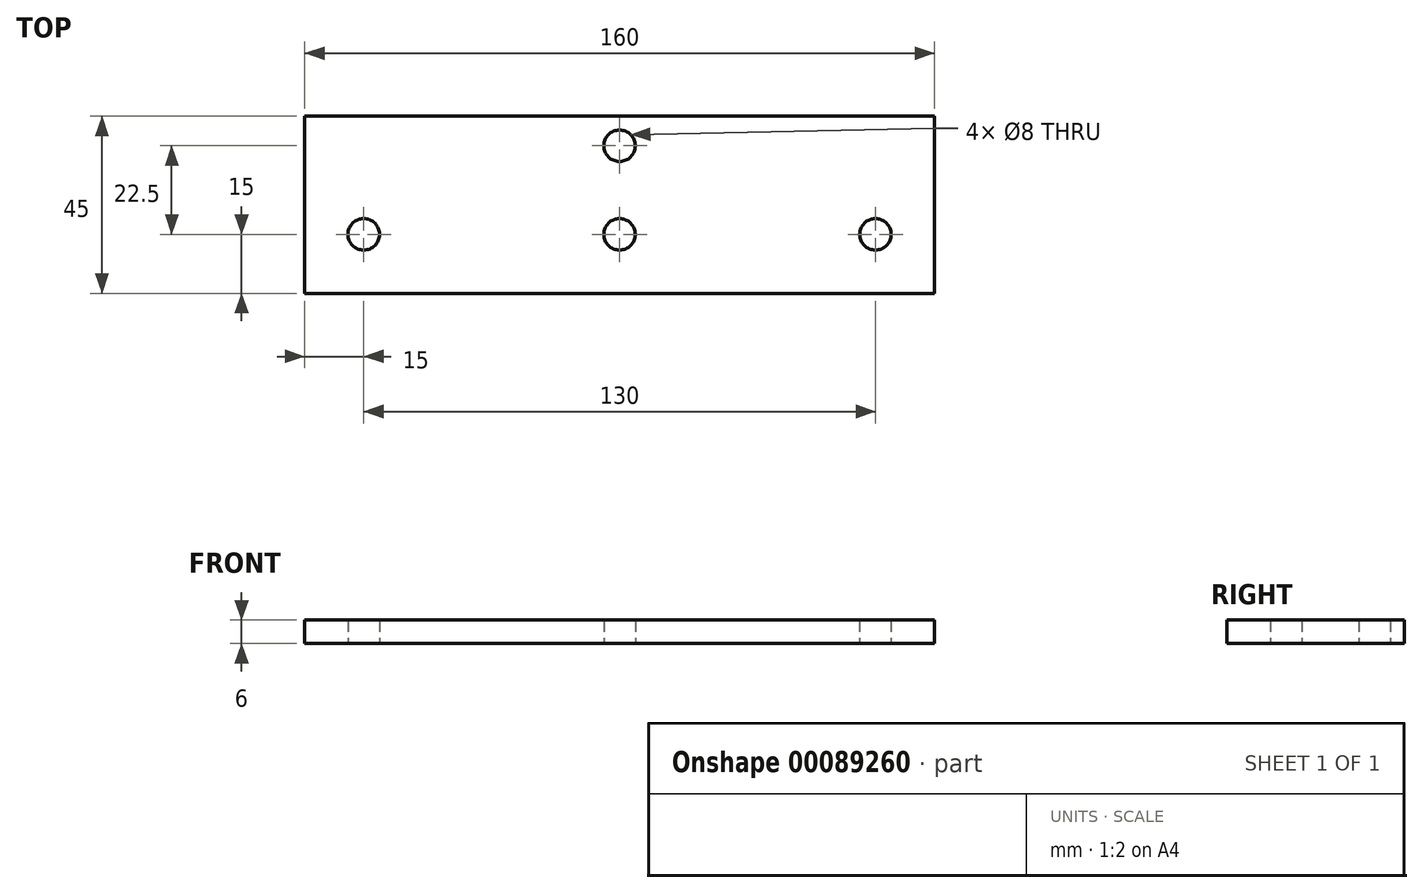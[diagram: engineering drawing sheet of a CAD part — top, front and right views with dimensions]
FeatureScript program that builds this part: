
annotation { "Feature Type Name" : "Feature", "Feature Type Description" : "" }
export const myFeature = defineFeature(function(context is Context, id is Id, definition is map)
    precondition{}
    {
        {
            var Q0;
            Q0=qCreatedBy(makeId("Top.planeOp"),FACE);
            var sketch = newSketch(context, id + "F0", { "sketchPlane" : qUnion([Q0])});
            skLineSegment(sketch, "E0.bottom", {"start": v(-80, 22.5) * mm, "end": v(80, 22.5) * mm});
            skLineSegment(sketch, "E0.top", {"start": v(-80, -22.5) * mm, "end": v(80, -22.5) * mm});
            skLineSegment(sketch, "E0.left", {"start": v(-80, 7.5) * mm, "end": v(-80, -22.5) * mm});
            skLineSegment(sketch, "E0.right", {"start": v(80, 7.5) * mm, "end": v(80, -22.5) * mm});
            skPoint(sketch, "E0.middle", {"position": v(0, 0) * mm});
            skLineSegment(sketch, "E1", {"start": v(-80, 22.5) * mm, "end": v(-80, 7.5) * mm});
            skLineSegment(sketch, "E2", {"start": v(80, 22.5) * mm, "end": v(80, 7.5) * mm});
            skPoint(sketch, "E3.orphan", {"position": v(-80, 22.5) * mm});
            skPoint(sketch, "E4.orphan", {"position": v(80, 22.5) * mm});
            skLineSegment(sketch, "E5", {"start": v(-80, -7.5) * mm, "end": v(80, -7.5) * mm, "construction": true});
            skCircle(sketch, "E6", {"center": v(-65, -7.5) * mm, "radius": 4 * mm});
            skCircle(sketch, "E7", {"center": v(65, -7.5) * mm, "radius": 4 * mm});
            skCircle(sketch, "E8", {"center": v(0, -7.5) * mm, "radius": 4 * mm});
            skCircle(sketch, "E9", {"center": v(0, 15) * mm, "radius": 4 * mm});
            skLineSegment(sketch, "E10", {"start": v(0, 22.5) * mm, "end": v(0, -22.5) * mm, "construction": true});
            skSolve(sketch);
        }
        {
            var Q0;
            Q0=makeQuery(id+"F0.imprint","IMPRINT",FACE,{"disambiguationData":[TD([[makeQuery(id+"F0.imprint","IMPRINT",EDGE,{"derivedFrom":sQuery(id+"F0.wireOp",EDGE,"E0.bottom")}),-1.0]])]});
            extrude(context, id + "F1", {"entities" : qUnion([Q0]), "depth" : 6 * mm});
        }
    });
